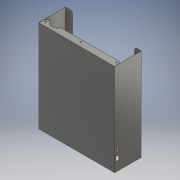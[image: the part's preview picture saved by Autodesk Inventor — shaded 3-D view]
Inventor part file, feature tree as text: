
AUTODESK INVENTOR PART (.ipt)
format: ipt  version: 2017 (Build 210142000, 142)  size: 309,760 bytes
history: native  units: mm
features: other x13, sheet_metal_op x10, sketch x9, reference x5, hole x2, chamfer x1, projected_geometry x1
ambient origin geometry x8: Origin, YZ Plane, XZ Plane, XY Plane, X Axis, Y Axis, Z Axis, Center Point
bodies: Solid1 (feature_tree)
feature tree (41):
  other  "Blocks"
  sheet_metal_op  "Face1"
  sheet_metal_op  "Flange1"
  sheet_metal_op  "Flange5"
  sheet_metal_op  "Flange6"
  chamfer  "Corner Round1"
  hole  "Hole1"  [1 undecoded]
  hole  "Hole2"  [1 undecoded]
  sketch  "Sketch1"  dims[d0=280.0mm d1=340.0mm]
  other  "Plate1"
  sketch  "Sketch2"  dims[d2=0.5mm d3=0.5mm]
  other  "Plate2"
  sheet_metal_op  "Bend1"
  sheet_metal_op  "Corner1"
  sketch  "Sketch6"  dims[d4=0.25mm]
  other  "Plate6"
  sheet_metal_op  "Bend5"
  sheet_metal_op  "Corner5"
  sketch  "Sketch7"  dims[d5=1.0mm]
  other  "Plate7"
  sheet_metal_op  "Bend6"
  sheet_metal_op  "Corner6"
  sketch  "Sketch8"  dims[d6=0.5mm]
  sketch  "Sketch9"  dims[d7=100.0mm d8=90.0deg d9=0.5mm]
  other  "lOGO"
  projected_geometry  "Projected Loop1"
  sketch  "Sketch10"  dims[d10=2.0mm]
  sketch  "Sketch11"  dims[d11=0.5mm]
  reference  "Reference1"
  sketch  "Sketch12"  dims[d12=0.5mm d43=0.5mm d44=0.25mm d45=1.0mm d46=0.5mm d47=25.0mm d48=90.0deg d49=0.5mm d50=2.0mm d51=0.5mm d52=0.5mm d53=0.5mm d54=0.25mm d55=1.0mm d56=0.5mm d57=25.0mm d58=90.0deg d59=0.5mm d60=2.0mm d61=0.5mm d62=0.5mm d63=8.0mm d64=5.15mm d65=6.0mm d66=4.0mm d67=2.0mm d68=90.0deg d69=0.5mm d70=20.594885mm d71=9.0mm d72=14.0mm d73=45.0deg d74=4.0mm d75=4.0mm d76=7.0mm d77=35.0mm d78=9.0mm d80=0.5mm d81=0.0mm d82=7.0mm d84=20.0mm d85=50.0mm d86=108.0mm d87=64.8mm d88=133.5mm d90=84.0mm d91=12.69mm d92=11.45mm d94=3.15mm d95=3.15mm d96=3.15mm d97=3.15mm d98=77.6mm d99=127.1mm d100=1.0mm d101=5.15mm d102=6.0mm d103=4.0mm d104=2.0mm d105=90.0deg d106=0.5mm d107=20.594885mm d108=10.0mm d112=40.0mm d113=0.5mm d114=0.0mm d115=0.5mm d116=0.5mm d117=12.0mm d118=5.0mm d119=0.3mm d120=0.0mm d121=0.5mm d122=0.0mm]
  reference  "Reference2"
  reference  "Reference3"
  reference  "Reference4"
  reference  "Reference5"
  other  "Cut1"
  other  "Cut2"
  other  "Cut3"
  parser-record x1  (decoder bookkeeping rows leaked as tree rows — omitted from the tree; the rows remain in map.json)
  other  "Espectometro.iam"
  other  "CorpoSplitter:2"
  other  "MB1137:1"
note: 2 required parameter values undecoded (feature->parameter linkage not recoverable at this tier; creation-order binding heuristic only, values carry confidence <= 0.55)
note: 1 file-system path scrubbed to <path> (originals preserved in map.json)
